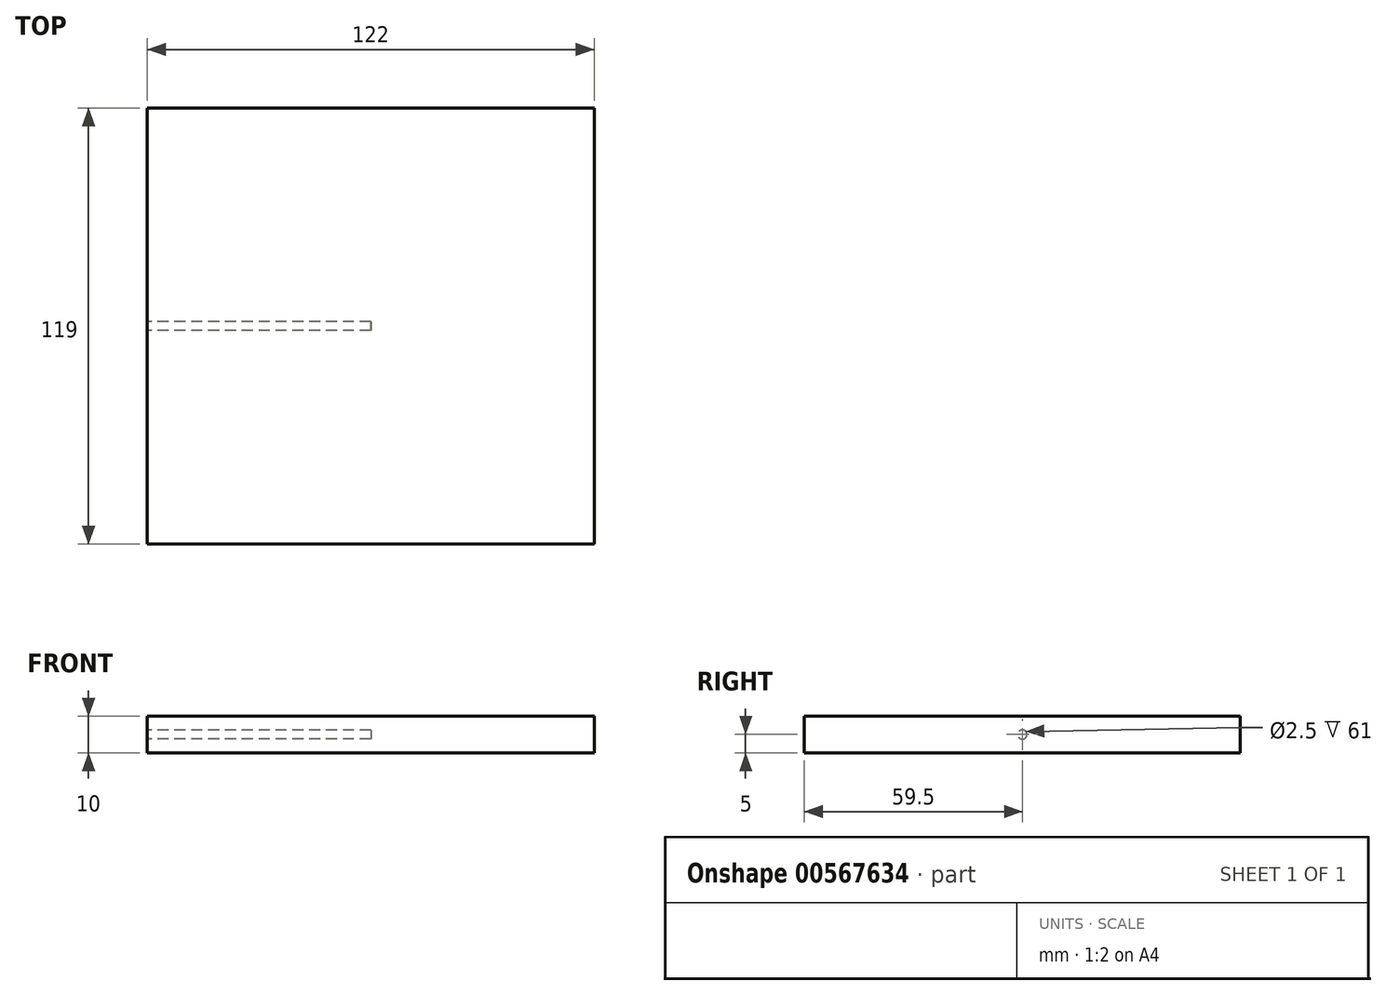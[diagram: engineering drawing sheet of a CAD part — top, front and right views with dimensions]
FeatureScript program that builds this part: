
annotation { "Feature Type Name" : "Feature", "Feature Type Description" : "" }
export const myFeature = defineFeature(function(context is Context, id is Id, definition is map)
    precondition{}
    {
        {
            var Q0;
            Q0=qCreatedBy(makeId("Top.planeOp"),FACE);
            var sketch = newSketch(context, id + "F0", { "sketchPlane" : qUnion([Q0])});
            skLineSegment(sketch, "E0.bottom", {"start": v(61, -59.5) * mm, "end": v(-61, -59.5) * mm});
            skLineSegment(sketch, "E0.top", {"start": v(61, 59.5) * mm, "end": v(-61, 59.5) * mm});
            skLineSegment(sketch, "E0.left", {"start": v(61, -59.5) * mm, "end": v(61, 59.5) * mm});
            skLineSegment(sketch, "E0.right", {"start": v(-61, -59.5) * mm, "end": v(-61, 59.5) * mm});
            skPoint(sketch, "E0.middle", {"position": v(0, 0) * mm});
            skSolve(sketch);
        }
        {
            var Q0;
            Q0 = qSketchRegion(id + "F0", true);
            extrude(context, id + "F1", {"entities" : qUnion([Q0]), "endBound" : BoundingType.SYMMETRIC, "depth" : 10 * mm, "offsetDistance" : 25 * mm});
        }
        {
            var Q0;
            Q0=makeQuery(id+"F1.opExtrude","SWEPT_FACE",FACE,{"disambiguationData":[OSD([sQuery(id+"F0.wireOp",EDGE,"E0.right")])]});
            var sketch = newSketch(context, id + "F2", { "sketchPlane" : qUnion([Q0])});
            skCircle(sketch, "E1", {"center": v(0, 0) * mm, "radius": 1.25 * mm});
            skSolve(sketch);
        }
        {
            var Q0;
            Q0 = qSketchRegion(id + "F2", true);
            extrude(context, id + "F3", {"entities" : qUnion([Q0]), "operationType" : NewBodyOperationType.REMOVE, "oppositeDirection" : true, "depth" : (122 / 2) * mm, "offsetDistance" : 25 * mm});
        }
    });
